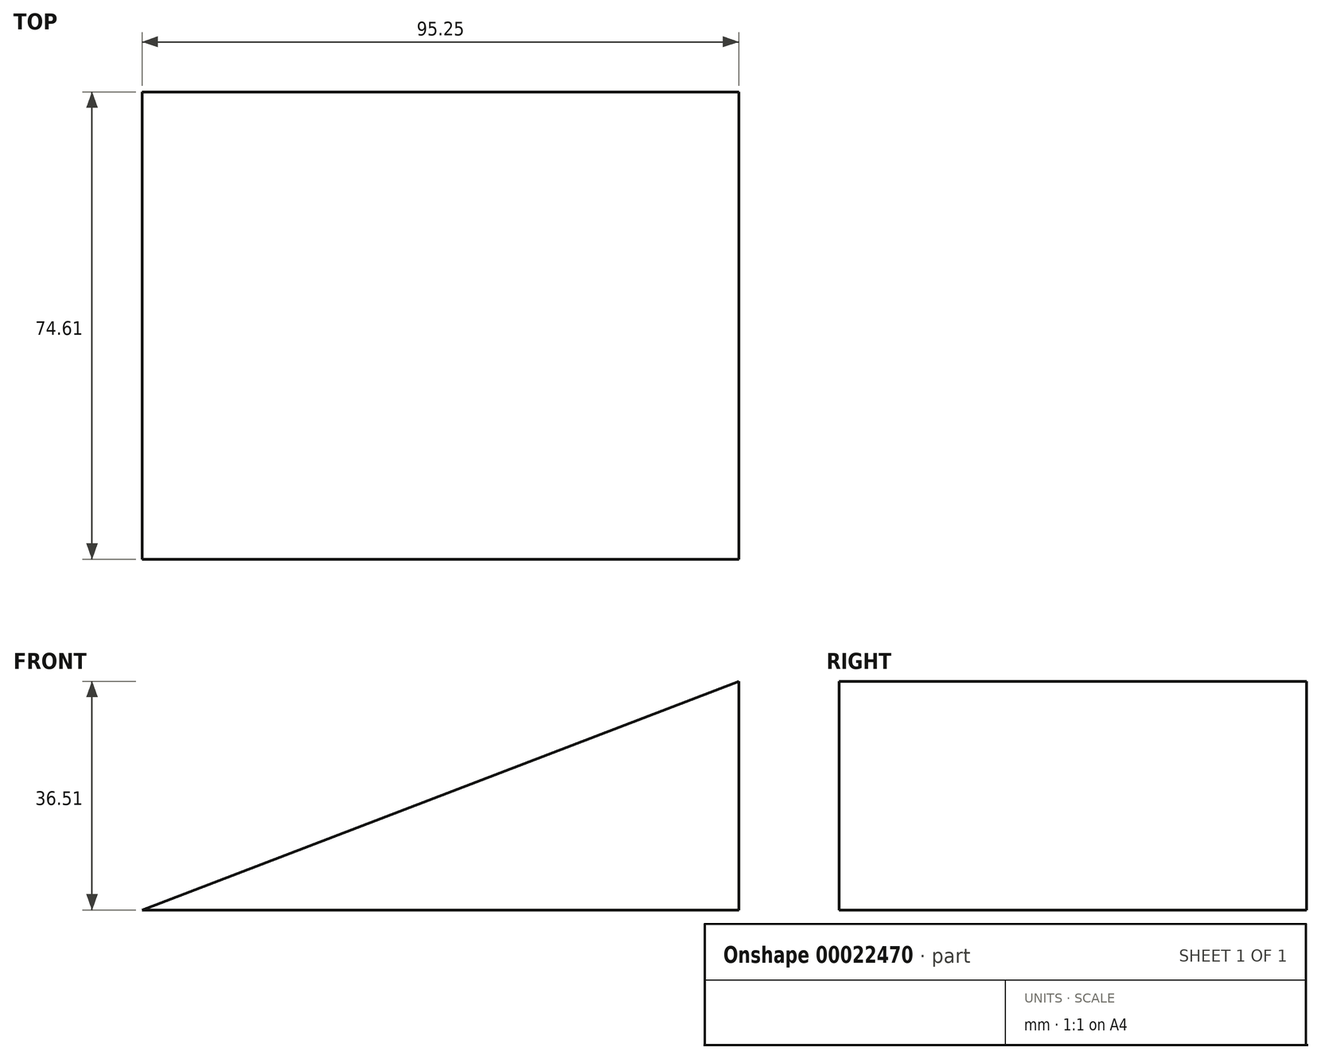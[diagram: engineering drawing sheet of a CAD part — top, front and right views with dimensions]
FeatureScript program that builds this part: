
annotation { "Feature Type Name" : "Feature", "Feature Type Description" : "" }
export const myFeature = defineFeature(function(context is Context, id is Id, definition is map)
    precondition{}
    {
        {
            var Q0;
            Q0=qCreatedBy(makeId("Front.planeOp"),FACE);
            var sketch = newSketch(context, id + "F0", { "sketchPlane" : qUnion([Q0])});
            skLineSegment(sketch, "E0", {"start": v(0, 0) * mm, "end": v(95.25, 0) * mm});
            skLineSegment(sketch, "E1", {"start": v(95.25, 0) * mm, "end": v(95.25, 36.51) * mm});
            skLineSegment(sketch, "E2", {"start": v(95.25, 36.51) * mm, "end": v(0, 0) * mm});
            skSolve(sketch);
        }
        {
            var Q0;
            Q0=makeQuery(id+"F0.imprint","IMPRINT",FACE,{"disambiguationData":[TD([[makeQuery(id+"F0.imprint","IMPRINT",EDGE,{"derivedFrom":sQuery(id+"F0.wireOp",EDGE,"E0")}),1.0]])]});
            extrude(context, id + "F1", {"entities" : qUnion([Q0]), "depth" : 38.1 * mm});
        }
        {
            var Q0;
            Q0 = qSketchRegion(id + "F0", true);
            var Q1;
            Q1=makeQuery(id+"F1.opExtrude","CAP_FACE",FACE,{"disambiguationData":[OSD([sQuery(id+"F0.wireOp",EDGE,"E0"),sQuery(id+"F0.wireOp",EDGE,"E1"),sQuery(id+"F0.wireOp",EDGE,"E2")])],"isStart":false});
            extrude(context, id + "F2", {"entities" : qUnion([Q0, Q1]), "operationType" : NewBodyOperationType.ADD, "depth" : 36.5 * mm});
        }
    });
